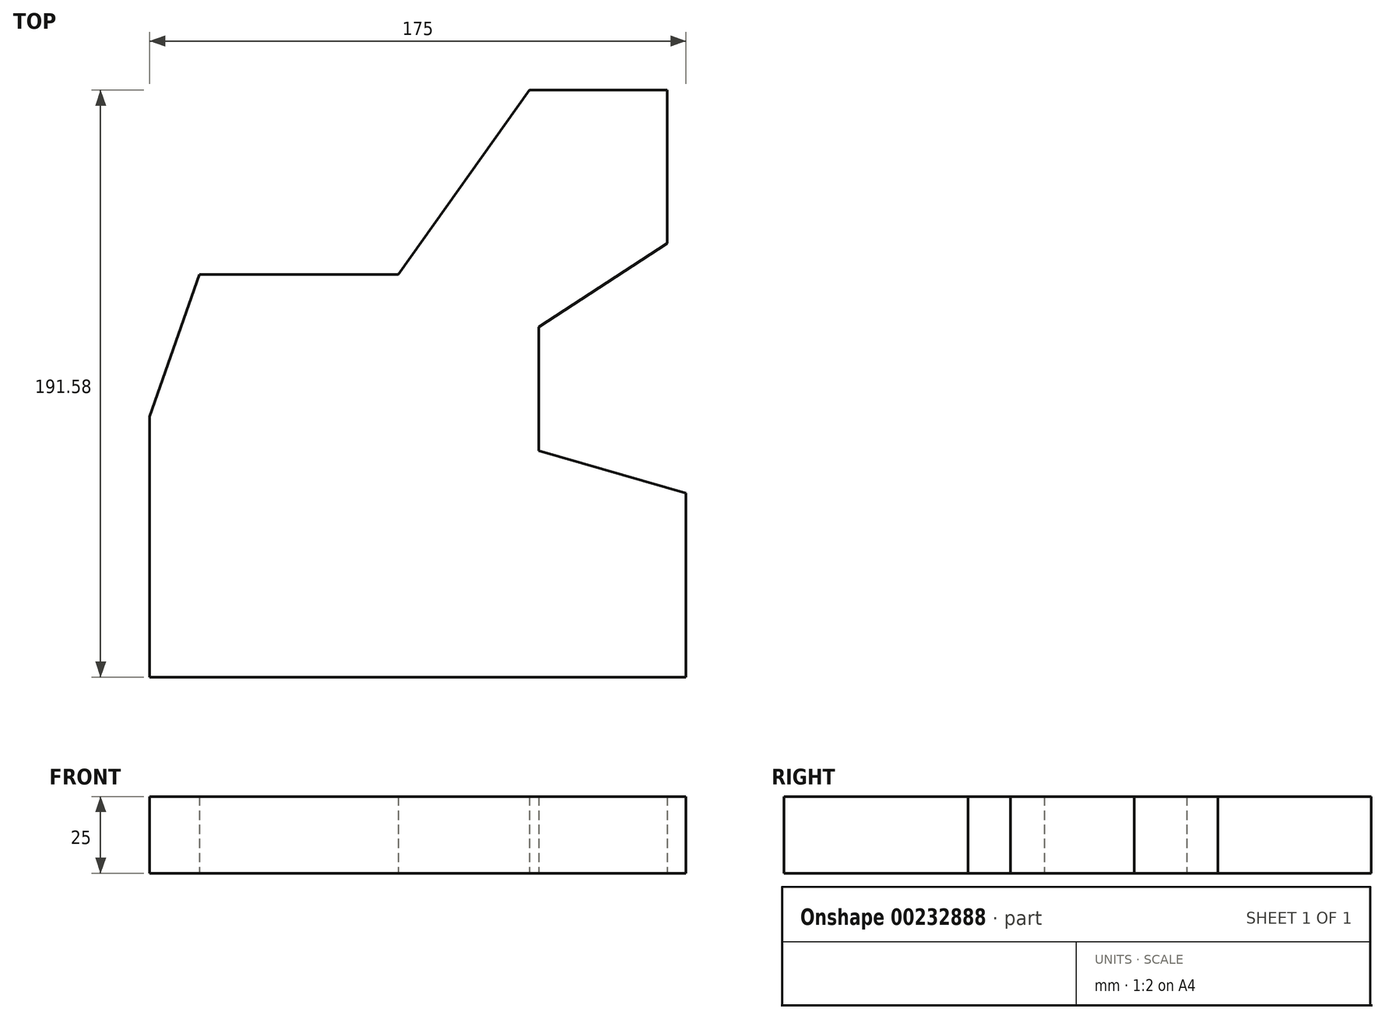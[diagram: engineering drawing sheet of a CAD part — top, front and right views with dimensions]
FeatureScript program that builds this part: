
annotation { "Feature Type Name" : "Feature", "Feature Type Description" : "" }
export const myFeature = defineFeature(function(context is Context, id is Id, definition is map)
    precondition{}
    {
        {
            var Q0;
            Q0=qCreatedBy(makeId("Top.planeOp"),FACE);
            var sketch = newSketch(context, id + "F0", { "sketchPlane" : qUnion([Q0])});
            skLineSegment(sketch, "E0", {"start": v(-96.25, -66.99) * mm, "end": v(78.75, -66.99) * mm});
            skLineSegment(sketch, "E1", {"start": v(-96.25, -66.99) * mm, "end": v(-96.25, 18.01) * mm});
            skLineSegment(sketch, "E2", {"start": v(-96.25, 18.01) * mm, "end": v(-80.1, 64.42) * mm});
            skLineSegment(sketch, "E3", {"start": v(-80.1, 64.42) * mm, "end": v(-15.1, 64.42) * mm});
            skLineSegment(sketch, "E4", {"start": v(-15.1, 64.42) * mm, "end": v(27.62, 124.6) * mm});
            skLineSegment(sketch, "E5", {"start": v(27.62, 124.6) * mm, "end": v(72.62, 124.6) * mm});
            skLineSegment(sketch, "E6", {"start": v(72.62, 124.6) * mm, "end": v(72.62, 74.6) * mm});
            skLineSegment(sketch, "E7", {"start": v(72.62, 74.6) * mm, "end": v(30.71, 47.32) * mm});
            skLineSegment(sketch, "E8", {"start": v(30.71, 47.32) * mm, "end": v(30.71, 6.87) * mm});
            skLineSegment(sketch, "E9", {"start": v(30.71, 6.87) * mm, "end": v(78.75, -6.99) * mm});
            skLineSegment(sketch, "E10", {"start": v(78.75, -6.99) * mm, "end": v(78.75, -66.99) * mm});
            skSolve(sketch);
        }
        {
            var Q0;
            Q0=makeQuery(id+"F0.imprint","IMPRINT",FACE,{"disambiguationData":[TD([[makeQuery(id+"F0.imprint","IMPRINT",EDGE,{"derivedFrom":sQuery(id+"F0.wireOp",EDGE,"E0")}),1.0]])]});
            extrude(context, id + "F1", {"entities" : qUnion([Q0]), "depth" : 25 * mm});
        }
    });
